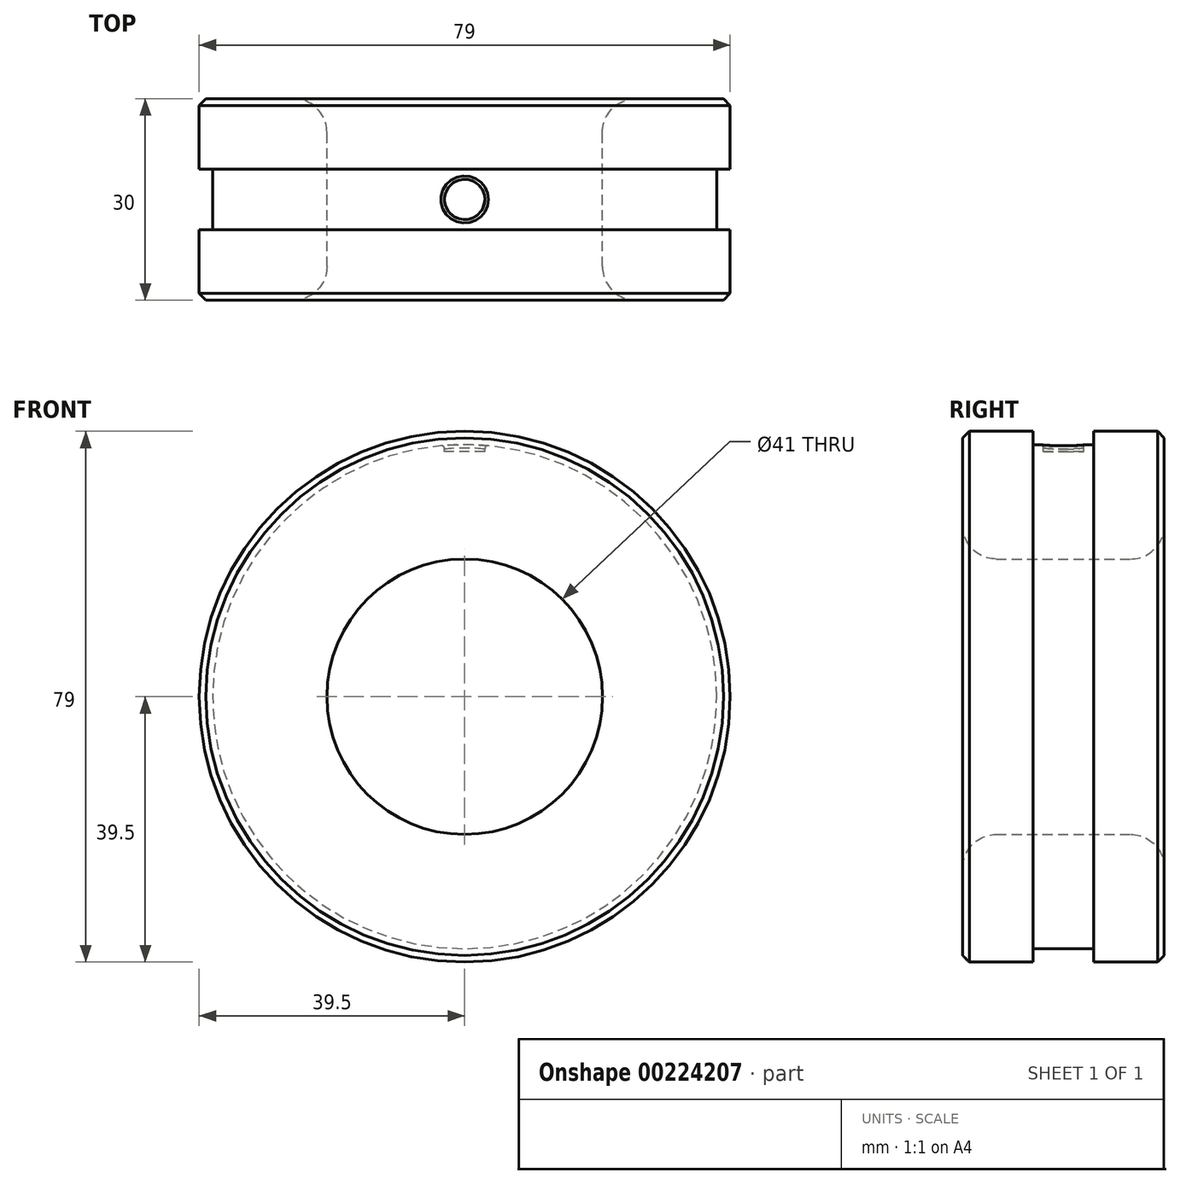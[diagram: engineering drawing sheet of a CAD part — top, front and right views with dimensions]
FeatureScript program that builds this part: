
annotation { "Feature Type Name" : "Feature", "Feature Type Description" : "" }
export const myFeature = defineFeature(function(context is Context, id is Id, definition is map)
    precondition{}
    {
        {
            var Q0;
            Q0=qCreatedBy(makeId("Front.planeOp"),FACE);
            var sketch = newSketch(context, id + "F0", { "sketchPlane" : qUnion([Q0])});
            skCircle(sketch, "E0", {"center": v(0, 0) * mm, "radius": 39.5 * mm});
            skCircle(sketch, "E1", {"center": v(0, 0) * mm, "radius": 20.5 * mm});
            skSolve(sketch);
        }
        {
            var Q0;
            Q0=makeQuery(id+"F0.imprint","IMPRINT",FACE,{"disambiguationData":[TD([[makeQuery(id+"F0.imprint","IMPRINT",EDGE,{"derivedFrom":sQuery(id+"F0.wireOp",EDGE,"E0")}),1.0]])]});
            extrude(context, id + "F1", {"entities" : qUnion([Q0]), "depth" : 30 * mm});
        }
        {
            var Q0;
            Q0=makeQuery(id+"F1.opExtrude","CAP_EDGE",EDGE,{"disambiguationData":[OSD([sQuery(id+"F0.wireOp",EDGE,"E1")])],"isStart":false});
            var Q1;
            Q1=makeQuery(id+"F1.opExtrude","CAP_EDGE",EDGE,{"disambiguationData":[OSD([sQuery(id+"F0.wireOp",EDGE,"E1")])],"isStart":true});
            fillet(context, id + "F2", {"entities" : qUnion([Q0, Q1]), "radius" : 5 * mm, "tangentPropagation" : true, "allowEdgeOverflow" : false});
        }
        {
            var Q0;
            Q0=qCreatedBy(makeId("Front.planeOp"),FACE);
            cPlane(context, id + "F3", {"entities" : qUnion([Q0]), "cplaneType" : CPlaneType.OFFSET, "offset" : 15 * mm, "width" : 150 * mm, "height" : 150 * mm});
        }
        {
            var Q0;
            Q0=qCreatedBy(id+"F3.planeOp",FACE);
            var sketch = newSketch(context, id + "F4", { "sketchPlane" : qUnion([Q0])});
            skCircle(sketch, "E2", {"center": v(0, 0) * mm, "radius": 37.5 * mm});
            skCircle(sketch, "E3", {"center": v(0, 0) * mm, "radius": 46.03 * mm});
            skSolve(sketch);
        }
        {
            var Q0;
            Q0 = qSketchRegion(id + "F4", true);
            extrude(context, id + "F5", {"entities" : qUnion([Q0]), "operationType" : NewBodyOperationType.REMOVE, "oppositeDirection" : true, "depth" : 4.5 * mm, "hasSecondDirection" : true, "secondDirectionOppositeDirection" : false, "secondDirectionDepth" : 4.5 * mm});
        }
        {
            var Q0;
            Q0=makeQuery(id+"F1.opExtrude","CAP_EDGE",EDGE,{"disambiguationData":[OSD([sQuery(id+"F0.wireOp",EDGE,"E0")])],"isStart":false});
            var Q1;
            Q1=makeQuery(id+"F1.opExtrude","CAP_EDGE",EDGE,{"disambiguationData":[OSD([sQuery(id+"F0.wireOp",EDGE,"E0")])],"isStart":true});
            chamfer(context, id + "F6", {"entities" : qUnion([Q0, Q1]), "width" : 1 * mm, "tangentPropagation" : true});
        }
        {
            var Q0;
            Q0=qCreatedBy(makeId("Top.planeOp"),FACE);
            cPlane(context, id + "F7", {"entities" : qUnion([Q0]), "cplaneType" : CPlaneType.OFFSET, "offset" : 37.5 * mm, "width" : 150 * mm, "height" : 150 * mm});
        }
        {
            var Q0;
            Q0=qCreatedBy(id+"F7.planeOp",FACE);
            var sketch = newSketch(context, id + "F8", { "sketchPlane" : qUnion([Q0])});
            skCircle(sketch, "E4", {"center": v(0, -15) * mm, "radius": 3 * mm});
            skSolve(sketch);
        }
        {
            var Q0;
            Q0 = qSketchRegion(id + "F8", true);
            extrude(context, id + "F9", {"entities" : qUnion([Q0]), "operationType" : NewBodyOperationType.REMOVE, "oppositeDirection" : true, "depth" : 1 * mm});
        }
        {
            var Q0;
            Q0=makeQuery(id+"F9.boolean.opBoolean","INTERSECT",EDGE,{"derivedFrom":[makeQuery(id+"F5.boolean.opBoolean","COPY",FACE,{"derivedFrom":makeQuery(id+"F5.opExtrude","SWEPT_FACE",FACE,{"disambiguationData":[OSD([sQuery(id+"F4.wireOp",EDGE,"E2")])]})}),makeQuery(id+"F9.opExtrude","SWEPT_FACE",FACE,{"disambiguationData":[OSD([sQuery(id+"F8.wireOp",EDGE,"E4")])]})]});
            fillet(context, id + "F10", {"entities" : qUnion([Q0]), "radius" : 0.5 * mm, "tangentPropagation" : true, "rho" : 0.5, "crossSection" : FilletCrossSection.CONIC, "allowEdgeOverflow" : false});
        }
    });
